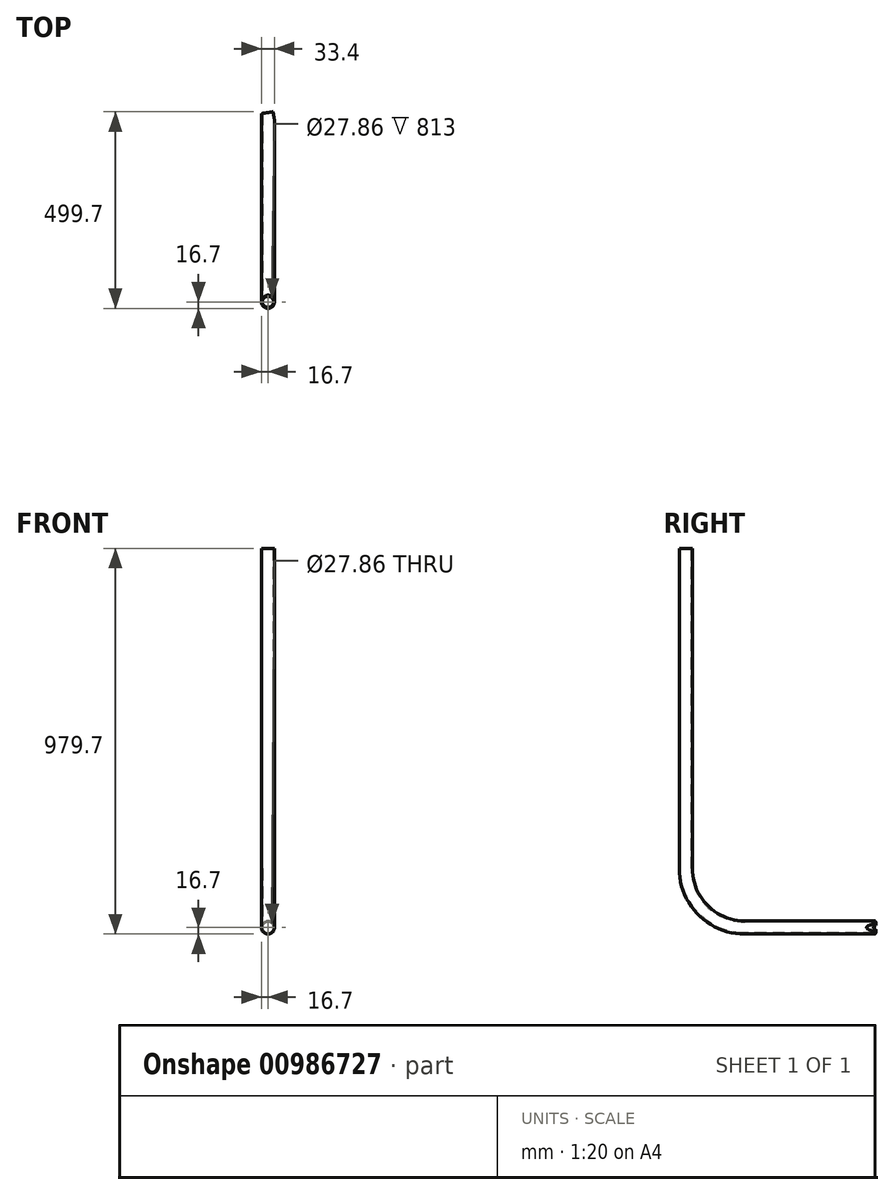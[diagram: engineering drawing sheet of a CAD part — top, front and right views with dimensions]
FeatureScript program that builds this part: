
annotation { "Feature Type Name" : "Feature", "Feature Type Description" : "" }
export const myFeature = defineFeature(function(context is Context, id is Id, definition is map)
    precondition{}
    {
        {
            var Q0;
            Q0=qCreatedBy(makeId("Right.planeOp"),FACE);
            var sketch = newSketch(context, id + "F0", { "sketchPlane" : qUnion([Q0])});
            skLineSegment(sketch, "E0", {"start": v(0, 0) * mm, "end": v(-333.6, 0) * mm});
            skLineSegment(sketch, "E1", {"start": v(-483.6, 150) * mm, "end": v(-483.6, 963) * mm});
            skPoint(sketch, "E2.visualSharp", {"position": v(-483.6, 0) * mm});
            skArc(sketch, "E2.filletArc", {"start": v(-483.6, 150) * mm, "mid": v(-439.67, 43.93) * mm, "end": v(-333.6, 0) * mm});
            skSolve(sketch);
        }
        {
            var Q0;
            Q0=qCreatedBy(makeId("Front.planeOp"),FACE);
            var sketch = newSketch(context, id + "F1", { "sketchPlane" : qUnion([Q0])});
            skCircle(sketch, "E3", {"center": v(0, 0) * mm, "radius": 16.7 * mm});
            skCircle(sketch, "E4.0", {"center": v(0, 0) * mm, "radius": 13.93 * mm});
            skSolve(sketch);
        }
        {
            var Q0;
            Q0=makeQuery(id+"F1.imprint","IMPRINT",FACE,{"disambiguationData":[TD([[makeQuery(id+"F1.imprint","IMPRINT",EDGE,{"derivedFrom":sQuery(id+"F1.wireOp",EDGE,"E3")}),1.0]])]});
            var Q1;
            Q1=sQuery(id+"F0.wireOp",EDGE,"E0");
            var Q2;
            Q2=sQuery(id+"F0.wireOp",EDGE,"E2.filletArc");
            var Q3;
            Q3=sQuery(id+"F0.wireOp",EDGE,"E1");
            sweep(context, id + "F2", {"profiles" : qUnion([Q0]), "path" : qUnion([Q1, Q2, Q3])});
        }
        {
            var Q0;
            Q0=qCreatedBy(makeId("Top.planeOp"),FACE);
            var sketch = newSketch(context, id + "F3", { "sketchPlane" : qUnion([Q0])});
            skLineSegment(sketch, "E5", {"start": v(0, 0) * mm, "end": v(16.7, 0) * mm});
            skLineSegment(sketch, "E6", {"start": v(16.7, 0) * mm, "end": v(16.7, -2.65) * mm});
            skLineSegment(sketch, "E7.MirrorCS", {"start": v(0, 0) * mm, "end": v(-29.63, 4.7) * mm});
            skLineSegment(sketch, "E8", {"start": v(-16.7, 2.65) * mm, "end": v(-16.7, 0) * mm});
            skLineSegment(sketch, "E9", {"start": v(-16.7, 0) * mm, "end": v(16.7, 0) * mm});
            skLineSegment(sketch, "E10", {"start": v(16.7, -5.47) * mm, "end": v(16.7, 0) * mm});
            skLineSegment(sketch, "E11", {"start": v(0, 0) * mm, "end": v(-16.7, 0) * mm});
            skLineSegment(sketch, "E12", {"start": v(-16.7, 0) * mm, "end": v(0, 0) * mm});
            skLineSegment(sketch, "E13", {"start": v(-16.7, 0) * mm, "end": v(-16.7, -32.2) * mm});
            skLineSegment(sketch, "E14.MirrorCS", {"start": v(-16.7, -5.47) * mm, "end": v(-16.7, 0) * mm});
            skLineSegment(sketch, "E15.MirrorCS", {"start": v(16.7, 0) * mm, "end": v(-16.7, 0) * mm});
            skLineSegment(sketch, "E16.MirrorCS", {"start": v(16.7, 0) * mm, "end": v(0, 0) * mm});
            skLineSegment(sketch, "E17.MirrorCS", {"start": v(16.7, 0) * mm, "end": v(16.7, -32.2) * mm});
            skLineSegment(sketch, "E18.MirrorCS", {"start": v(-16.7, -5.3) * mm, "end": v(12.93, -0.6) * mm});
            skLineSegment(sketch, "E19.MirrorCS", {"start": v(12.93, -0.6) * mm, "end": v(19.43, -41.61) * mm});
            skSolve(sketch);
        }
        {
            var Q0;
            Q0 = qSketchRegion(id + "F3", true);
            extrude(context, id + "F4", {"entities" : qUnion([Q0]), "operationType" : NewBodyOperationType.REMOVE, "endBound" : BoundingType.THROUGH_ALL, "oppositeDirection" : true, "depth" : 25 * mm, "offsetDistance" : 25 * mm, "hasSecondDirection" : true, "secondDirectionBound" : BoundingType.THROUGH_ALL, "secondDirectionOppositeDirection" : false, "secondDirectionDepth" : 25 * mm});
        }
    });
